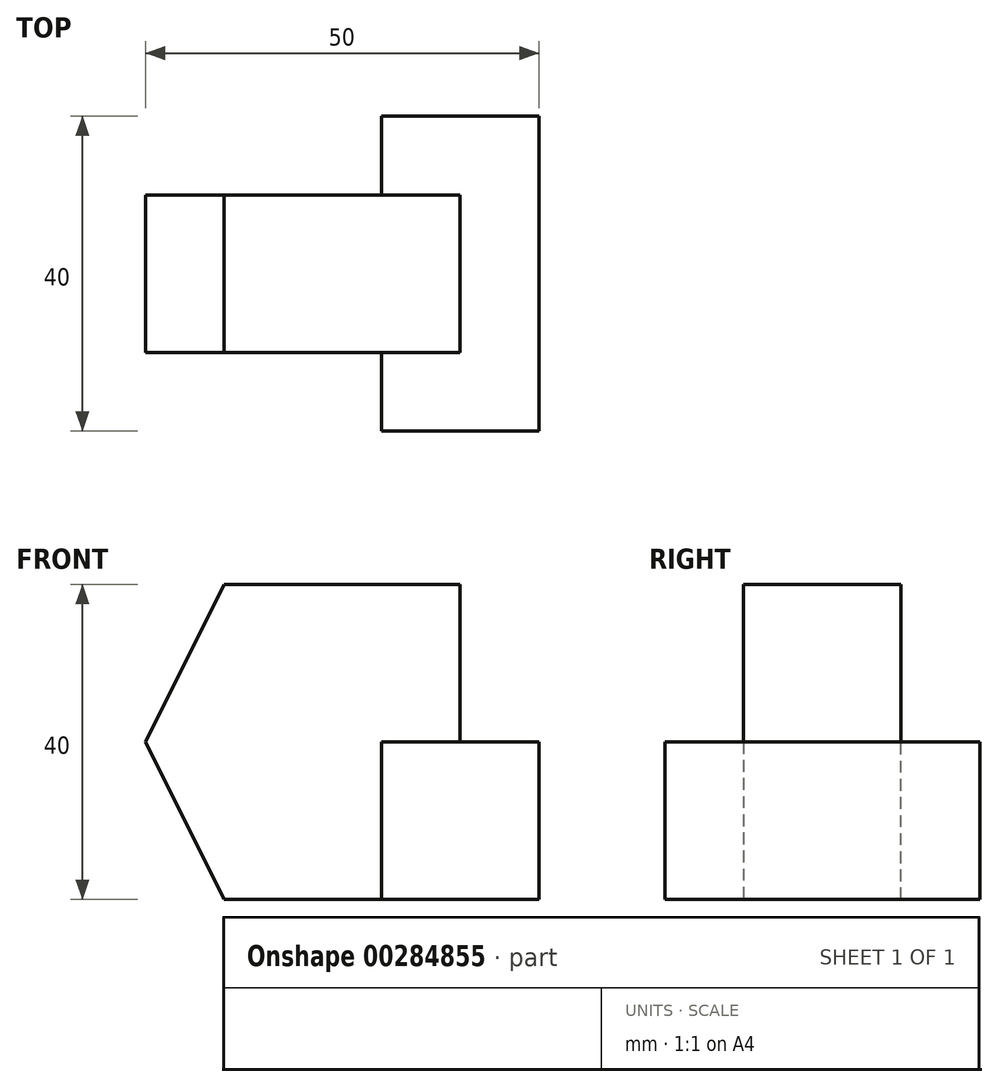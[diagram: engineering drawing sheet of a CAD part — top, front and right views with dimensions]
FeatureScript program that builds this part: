
annotation { "Feature Type Name" : "Feature", "Feature Type Description" : "" }
export const myFeature = defineFeature(function(context is Context, id is Id, definition is map)
    precondition{}
    {
        {
            var Q0;
            Q0=qCreatedBy(makeId("Front.planeOp"),FACE);
            var sketch = newSketch(context, id + "F0", { "sketchPlane" : qUnion([Q0])});
            skLineSegment(sketch, "E0.bottom", {"start": v(0, 0) * mm, "end": v(50, 0) * mm});
            skLineSegment(sketch, "E0.top", {"start": v(0, 40) * mm, "end": v(50, 40) * mm});
            skLineSegment(sketch, "E0.left", {"start": v(0, 0) * mm, "end": v(0, 40) * mm});
            skLineSegment(sketch, "E0.right", {"start": v(50, 0) * mm, "end": v(50, 40) * mm});
            skSolve(sketch);
        }
        {
            var Q0;
            Q0=makeQuery(id+"F0.imprint","IMPRINT",FACE,{"disambiguationData":[TD([[makeQuery(id+"F0.imprint","IMPRINT",EDGE,{"derivedFrom":sQuery(id+"F0.wireOp",EDGE,"E0.bottom")}),1.0]])]});
            extrude(context, id + "F1", {"entities" : qUnion([Q0]), "depth" : 40 * mm});
        }
        {
            var Q0;
            Q0=makeQuery(id+"F1.opExtrude","SWEPT_FACE",FACE,{"disambiguationData":[OSD([sQuery(id+"F0.wireOp",EDGE,"E0.left")])]});
            var sketch = newSketch(context, id + "F2", { "sketchPlane" : qUnion([Q0])});
            skLineSegment(sketch, "E1", {"start": v(0, 20) * mm, "end": v(40, 20) * mm});
            skLineSegment(sketch, "E2", {"start": v(30, 40) * mm, "end": v(30, 20) * mm});
            skLineSegment(sketch, "E3", {"start": v(10, 40) * mm, "end": v(10, 20) * mm});
            skLineSegment(sketch, "E4.0", {"start": v(40, 40) * mm, "end": v(0, 40) * mm});
            skLineSegment(sketch, "E5.0.1", {"start": v(40, 40) * mm, "end": v(40, 20) * mm});
            skLineSegment(sketch, "E5.0.3", {"start": v(40, 20) * mm, "end": v(40, 40) * mm});
            skLineSegment(sketch, "E6.0.1", {"start": v(0, 40) * mm, "end": v(0, 20) * mm});
            skLineSegment(sketch, "E6.0.3", {"start": v(0, 0) * mm, "end": v(0, 40) * mm});
            skPoint(sketch, "E7.orphan", {"position": v(40, 0) * mm});
            skPoint(sketch, "E8.orphan", {"position": v(0, 0) * mm});
            skSolve(sketch);
        }
        {
            var Q0;
            {var subQ3=sQuery(id+"F2.wireOp",EDGE,"E3");Q0=makeQuery(id+"F2.imprint","IMPRINT",FACE,{"disambiguationData":[TD([[makeQuery(id+"F2.imprint","IMPRINT",EDGE,{"derivedFrom":subQ3}),-1.0]])]});}
            var Q1;
            {var subQ2=sQuery(id+"F2.wireOp",EDGE,"E2");Q1=makeQuery(id+"F2.imprint","IMPRINT",FACE,{"disambiguationData":[TD([[makeQuery(id+"F2.imprint","IMPRINT",EDGE,{"derivedFrom":subQ2}),1.0]])]});}
            extrude(context, id + "F3", {"entities" : qUnion([Q0, Q1]), "operationType" : NewBodyOperationType.REMOVE, "endBound" : BoundingType.THROUGH_ALL, "oppositeDirection" : true, "depth" : 30 * mm});
        }
        {
            var Q0;
            {var subQ0=sQuery(id+"F2.wireOp",EDGE,"E1");Q0=makeQuery(id+"F3.boolean.opBoolean","COPY",FACE,{"derivedFrom":makeQuery(id+"F3.opExtrude","SWEPT_FACE",FACE,{"disambiguationData":[OSD([subQ0]),TDD([makeQuery(id+"F2.imprint","IMPRINT",EDGE,{"disambiguationData":[TD([[makeQuery(id+"F2.imprint","INTERSECT",VERTEX,{"derivedFrom":[subQ0,sQuery(id+"F2.wireOp",EDGE,"E6.0.3")]}),-1.0]])],"derivedFrom":subQ0})])]})});}
            var sketch = newSketch(context, id + "F4", { "sketchPlane" : qUnion([Q0])});
            skLineSegment(sketch, "E9.0", {"start": v(50, 0) * mm, "end": v(30, 0) * mm});
            skLineSegment(sketch, "E10.0", {"start": v(50, -10) * mm, "end": v(30, -10) * mm});
            skLineSegment(sketch, "E11.0", {"start": v(50, -30) * mm, "end": v(30, -30) * mm});
            skLineSegment(sketch, "E12.0", {"start": v(50, -40) * mm, "end": v(30, -40) * mm});
            skLineSegment(sketch, "E13", {"start": v(30, 0) * mm, "end": v(30, -10) * mm});
            skLineSegment(sketch, "E14", {"start": v(30, -30) * mm, "end": v(30, -40) * mm});
            skLineSegment(sketch, "E15.0", {"start": v(50, -30) * mm, "end": v(50, -40) * mm});
            skLineSegment(sketch, "E16.0", {"start": v(50, 0) * mm, "end": v(50, -10) * mm});
            skPoint(sketch, "E17.orphan", {"position": v(0, -10) * mm});
            skPoint(sketch, "E18.orphan", {"position": v(0, -30) * mm});
            skPoint(sketch, "E19.orphan", {"position": v(0, -40) * mm});
            skPoint(sketch, "E20.orphan", {"position": v(0, 0) * mm});
            skLineSegment(sketch, "E21.0", {"start": v(50, 0) * mm, "end": v(0, 0) * mm});
            skLineSegment(sketch, "E22.0", {"start": v(50, -10) * mm, "end": v(0, -10) * mm});
            skLineSegment(sketch, "E23.0", {"start": v(0, 0) * mm, "end": v(0, -10) * mm});
            skLineSegment(sketch, "E24.0", {"start": v(0, -30) * mm, "end": v(0, -40) * mm});
            skLineSegment(sketch, "E25.0", {"start": v(50, -40) * mm, "end": v(0, -40) * mm});
            skLineSegment(sketch, "E26.0", {"start": v(50, -30) * mm, "end": v(0, -30) * mm});
            skSolve(sketch);
        }
        {
            var Q0;
            {var subQ0=sQuery(id+"F4.wireOp",EDGE,"E13");Q0=makeQuery(id+"F4.imprint","IMPRINT",FACE,{"disambiguationData":[TD([[makeQuery(id+"F4.imprint","IMPRINT",EDGE,{"derivedFrom":subQ0}),-1.0]])]});}
            var Q1;
            {var subQ0=sQuery(id+"F4.wireOp",EDGE,"E14");Q1=makeQuery(id+"F4.imprint","IMPRINT",FACE,{"disambiguationData":[TD([[makeQuery(id+"F4.imprint","IMPRINT",EDGE,{"derivedFrom":subQ0}),-1.0]])]});}
            extrude(context, id + "F5", {"entities" : qUnion([Q0, Q1]), "operationType" : NewBodyOperationType.REMOVE, "endBound" : BoundingType.THROUGH_ALL, "oppositeDirection" : true, "depth" : 25 * mm});
        }
        {
            var Q0;
            Q0=makeQuery(id+"F1.opExtrude","SWEPT_FACE",FACE,{"disambiguationData":[OSD([sQuery(id+"F0.wireOp",EDGE,"E0.top")])]});
            var sketch = newSketch(context, id + "F6", { "sketchPlane" : qUnion([Q0])});
            skLineSegment(sketch, "E27", {"start": v(40, -10) * mm, "end": v(40, -30) * mm});
            skLineSegment(sketch, "E28.0", {"start": v(50, -10) * mm, "end": v(0, -10) * mm});
            skLineSegment(sketch, "E29.0", {"start": v(50, -30) * mm, "end": v(50, -10) * mm});
            skLineSegment(sketch, "E30.0", {"start": v(50, -30) * mm, "end": v(0, -30) * mm});
            skSolve(sketch);
        }
        {
            var Q0;
            Q0=qSketchRegion(id+"F6",true);
            var Q1;
            {var subQ0=sQuery(id+"F2.wireOp",EDGE,"E1");Q1=makeQuery(id+"F3.boolean.opBoolean","COPY",FACE,{"derivedFrom":makeQuery(id+"F3.opExtrude","SWEPT_FACE",FACE,{"disambiguationData":[OSD([subQ0]),TDD([makeQuery(id+"F2.imprint","IMPRINT",EDGE,{"disambiguationData":[TD([[makeQuery(id+"F2.imprint","INTERSECT",VERTEX,{"derivedFrom":[subQ0,sQuery(id+"F2.wireOp",EDGE,"E6.0.3")]}),-1.0]])],"derivedFrom":subQ0})])]})});}
            extrude(context, id + "F7", {"entities" : qUnion([Q0]), "operationType" : NewBodyOperationType.REMOVE, "endBound" : BoundingType.UP_TO_SURFACE, "oppositeDirection" : true, "endBoundEntityFace" : qUnion([Q1]), "depth" : 25 * mm});
        }
        {
            var Q0;
            Q0=makeQuery(id+"F5.boolean.opBoolean","MERGE",FACE,{"derivedFrom":[makeQuery(id+"F3.boolean.opBoolean","COPY",FACE,{"derivedFrom":makeQuery(id+"F3.opExtrude","SWEPT_FACE",FACE,{"disambiguationData":[OSD([sQuery(id+"F2.wireOp",EDGE,"E2")])]})}),makeQuery(id+"F5.opExtrude","SWEPT_FACE",FACE,{"disambiguationData":[OSD([sQuery(id+"F4.wireOp",EDGE,"E26.0")])]})]});
            var sketch = newSketch(context, id + "F8", { "sketchPlane" : qUnion([Q0])});
            skLineSegment(sketch, "E31.bottom", {"start": v(0, 40) * mm, "end": v(10, 40) * mm});
            skLineSegment(sketch, "E31.top", {"start": v(0, 20) * mm, "end": v(10, 20) * mm});
            skLineSegment(sketch, "E31.left", {"start": v(0, 40) * mm, "end": v(0, 20) * mm});
            skLineSegment(sketch, "E31.right", {"start": v(10, 40) * mm, "end": v(10, 20) * mm});
            skLineSegment(sketch, "E32", {"start": v(10, 40) * mm, "end": v(0, 20) * mm});
            skLineSegment(sketch, "E33", {"start": v(0, 20) * mm, "end": v(10, 0) * mm});
            skLineSegment(sketch, "E34", {"start": v(10, 0) * mm, "end": v(0, 0) * mm});
            skLineSegment(sketch, "E35", {"start": v(0, 0) * mm, "end": v(0, 20) * mm});
            skSolve(sketch);
        }
        {
            var Q0;
            Q0=makeQuery(id+"F8.imprint","IMPRINT",FACE,{"disambiguationData":[TD([[makeQuery(id+"F8.imprint","IMPRINT",EDGE,{"derivedFrom":sQuery(id+"F8.wireOp",EDGE,"E31.bottom")}),1.0]])]});
            extrude(context, id + "F9", {"entities" : qUnion([Q0]), "operationType" : NewBodyOperationType.REMOVE, "endBound" : BoundingType.THROUGH_ALL, "oppositeDirection" : true, "depth" : 25 * mm});
        }
        {
            var Q0;
            Q0=makeQuery(id+"F8.imprint","IMPRINT",FACE,{"disambiguationData":[TD([[makeQuery(id+"F8.imprint","IMPRINT",EDGE,{"derivedFrom":sQuery(id+"F8.wireOp",EDGE,"E33")}),-1.0]])]});
            extrude(context, id + "F10", {"entities" : qUnion([Q0]), "operationType" : NewBodyOperationType.REMOVE, "endBound" : BoundingType.THROUGH_ALL, "oppositeDirection" : true, "depth" : 25 * mm});
        }
    });
